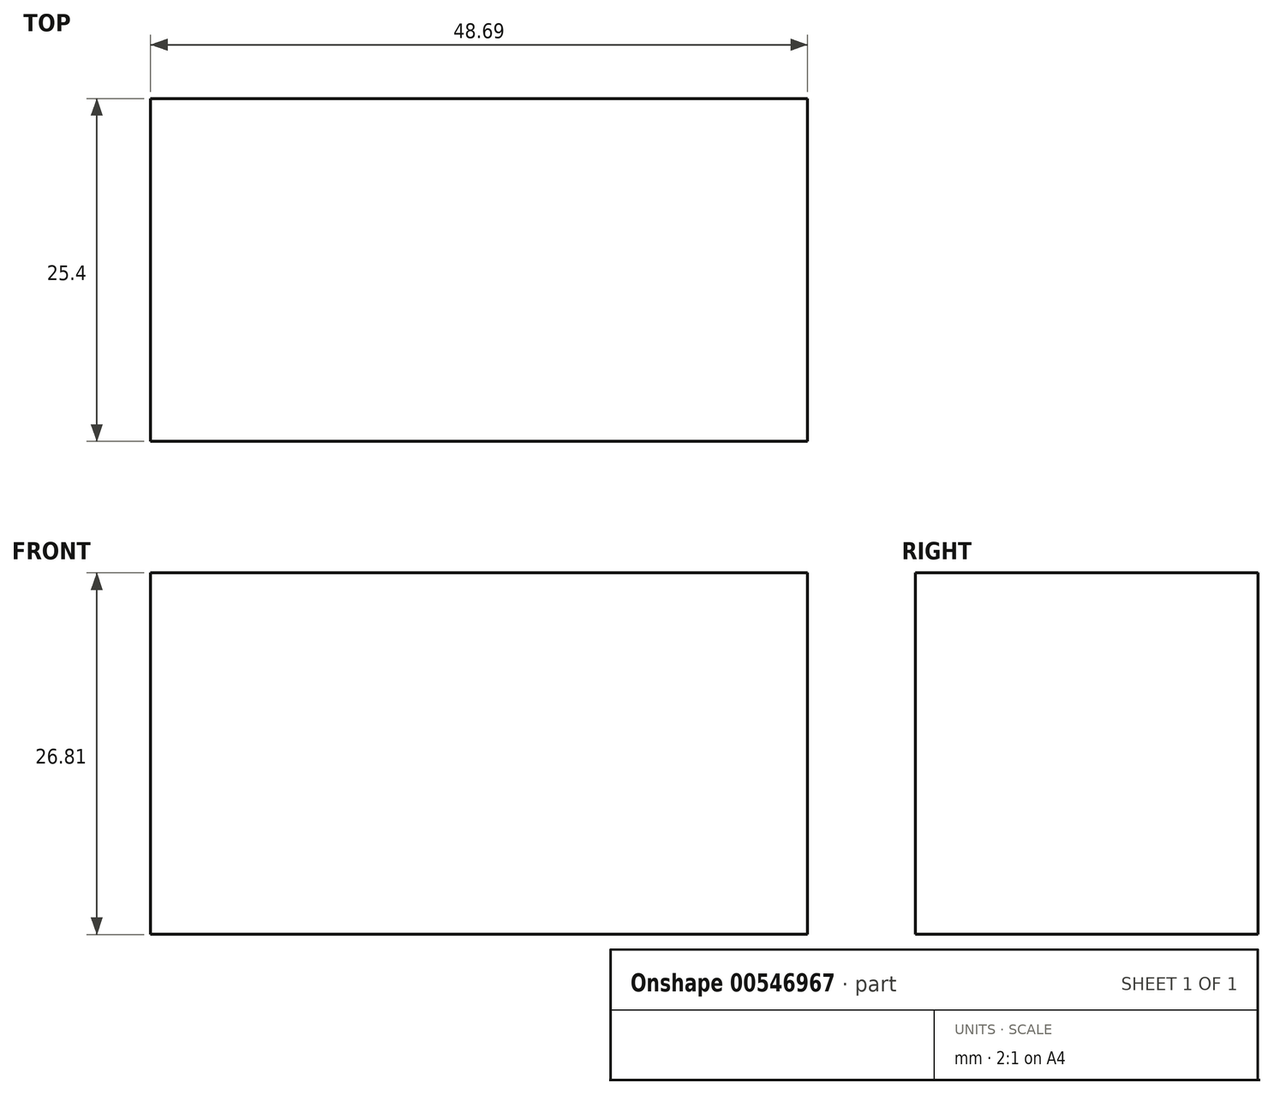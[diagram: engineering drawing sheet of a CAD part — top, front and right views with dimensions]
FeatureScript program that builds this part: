
annotation { "Feature Type Name" : "Feature", "Feature Type Description" : "" }
export const myFeature = defineFeature(function(context is Context, id is Id, definition is map)
    precondition{}
    {
        {
            var Q0;
            Q0=qCreatedBy(makeId("Front.planeOp"),FACE);
            var sketch = newSketch(context, id + "F0", { "sketchPlane" : qUnion([Q0])});
            skLineSegment(sketch, "E0.bottom", {"start": v(-63.45, 58.1) * mm, "end": v(-14.76, 58.1) * mm});
            skLineSegment(sketch, "E0.top", {"start": v(-63.45, 31.3) * mm, "end": v(-14.76, 31.3) * mm});
            skLineSegment(sketch, "E0.left", {"start": v(-63.45, 58.1) * mm, "end": v(-63.45, 31.3) * mm});
            skLineSegment(sketch, "E0.right", {"start": v(-14.76, 58.1) * mm, "end": v(-14.76, 31.3) * mm});
            skSolve(sketch);
        }
        {
            var Q0;
            Q0 = qSketchRegion(id + "F0", true);
            extrude(context, id + "F1", {"entities" : qUnion([Q0]), "depth" : 25.4 * mm, "offsetDistance" : 25.4 * mm});
        }
        {
            var Q0;
            Q0=qCreatedBy(makeId("Front.planeOp"),FACE);
            var sketch = newSketch(context, id + "F2", { "sketchPlane" : qUnion([Q0])});
            skCircle(sketch, "E1", {"center": v(37.38, 44.06) * mm, "radius": 14.91 * mm});
            skSolve(sketch);
        }
        {
            var Q0;
            Q0=qCreatedBy(makeId("Front.planeOp"),FACE);
            cPlane(context, id + "F3", {"entities" : qUnion([Q0]), "cplaneType" : CPlaneType.OFFSET, "offset" : 25.4 * mm, "width" : 152.4 * mm, "height" : 152.4 * mm});
        }
        {
            var Q0;
            Q0=qCreatedBy(id+"F3.planeOp",FACE);
            cPlane(context, id + "F4", {"entities" : qUnion([Q0]), "cplaneType" : CPlaneType.OFFSET, "offset" : 25.4 * mm, "width" : 152.4 * mm, "height" : 152.4 * mm});
        }
        {
            var Q0;
            Q0=qCreatedBy(id+"F3.planeOp",FACE);
            var sketch = newSketch(context, id + "F5", { "sketchPlane" : qUnion([Q0])});
            skLineSegment(sketch, "E2.bottom", {"start": v(23.18, 60.07) * mm, "end": v(58.45, 60.07) * mm});
            skLineSegment(sketch, "E2.top", {"start": v(23.18, 26.33) * mm, "end": v(58.45, 26.33) * mm});
            skLineSegment(sketch, "E2.left", {"start": v(23.18, 60.07) * mm, "end": v(23.18, 26.33) * mm});
            skLineSegment(sketch, "E2.right", {"start": v(58.45, 60.07) * mm, "end": v(58.45, 26.33) * mm});
            skSolve(sketch);
        }
        {
            var Q0;
            Q0=qCreatedBy(id+"F4.planeOp",FACE);
            var sketch = newSketch(context, id + "F6", { "sketchPlane" : qUnion([Q0])});
            skCircle(sketch, "E3", {"center": v(37.55, 49.96) * mm, "radius": 20.26 * mm});
            skSolve(sketch);
        }
        {
            var Q0;
            Q0=makeQuery(id+"F2.imprint","IMPRINT",FACE,{"disambiguationData":[TD([[makeQuery(id+"F2.imprint","IMPRINT",EDGE,{"derivedFrom":sQuery(id+"F2.wireOp",EDGE,"E1")}),1.0]])]});
            var Q1;
            Q1=makeQuery(id+"F5.imprint","IMPRINT",FACE,{"disambiguationData":[TD([[makeQuery(id+"F5.imprint","IMPRINT",EDGE,{"derivedFrom":sQuery(id+"F5.wireOp",EDGE,"E2.bottom")}),-1.0]])]});
            var Q2;
            Q2=makeQuery(id+"F6.imprint","IMPRINT",FACE,{"disambiguationData":[TD([[makeQuery(id+"F6.imprint","IMPRINT",EDGE,{"derivedFrom":sQuery(id+"F6.wireOp",EDGE,"E3")}),1.0]])]});
            var Q3;
            Q3=makeQuery(id+"F2.imprint","IMPRINT",FACE,{"disambiguationData":[TD([[makeQuery(id+"F2.imprint","IMPRINT",EDGE,{"derivedFrom":sQuery(id+"F2.wireOp",EDGE,"E1")}),1.0]])]});
            var Q4;
            Q4=makeQuery(id+"F5.imprint","IMPRINT",FACE,{"disambiguationData":[TD([[makeQuery(id+"F5.imprint","IMPRINT",EDGE,{"derivedFrom":sQuery(id+"F5.wireOp",EDGE,"E2.bottom")}),-1.0]])]});
            var Q5;
            Q5=makeQuery(id+"F6.imprint","IMPRINT",FACE,{"disambiguationData":[TD([[makeQuery(id+"F6.imprint","IMPRINT",EDGE,{"derivedFrom":sQuery(id+"F6.wireOp",EDGE,"E3")}),1.0]])]});
            loft(context, id + "F7", {"bodyType" : ToolBodyType.SURFACE, "sheetProfilesArray" : [{ "sheetProfileEntities" : qUnion([Q0]) }, { "sheetProfileEntities" : qUnion([Q1]) }, { "sheetProfileEntities" : qUnion([Q2]) }], "wireProfilesArray" : [{ "wireProfileEntities" : qUnion([Q3]) }, { "wireProfileEntities" : qUnion([Q4]) }, { "wireProfileEntities" : qUnion([Q5]) }]});
        }
    });
